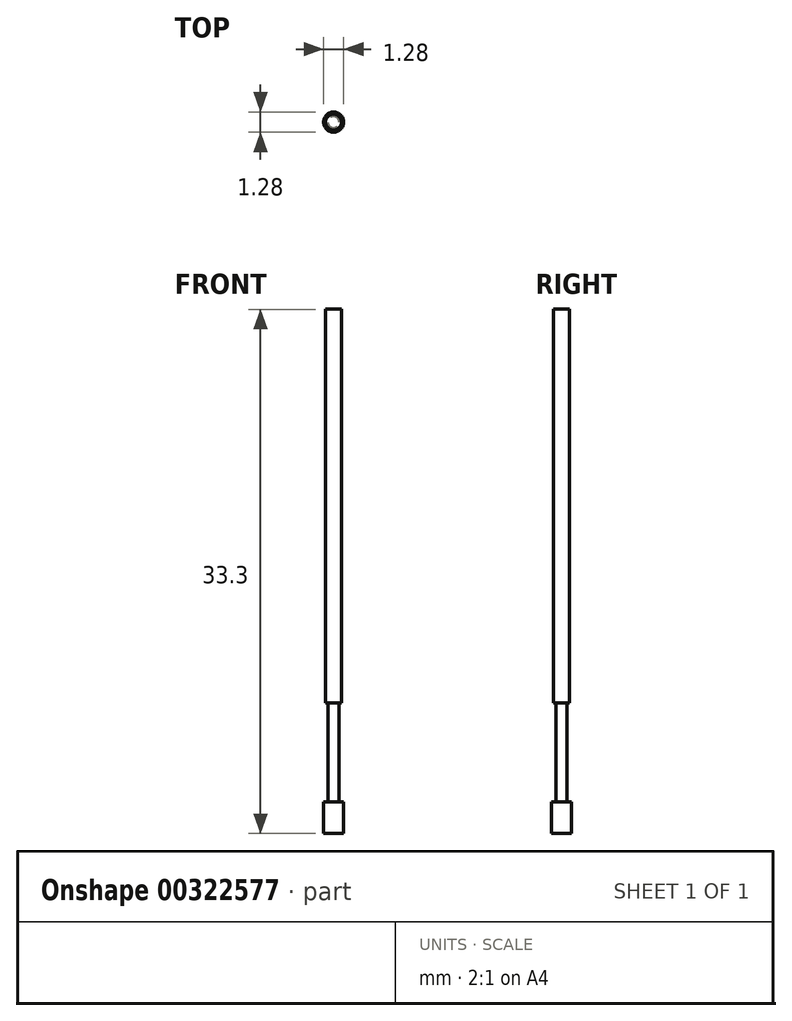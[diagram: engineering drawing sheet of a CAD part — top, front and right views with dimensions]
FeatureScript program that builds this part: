
annotation { "Feature Type Name" : "Feature", "Feature Type Description" : "" }
export const myFeature = defineFeature(function(context is Context, id is Id, definition is map)
    precondition{}
    {
        {
            var Q0;
            Q0=qCreatedBy(makeId("Top.planeOp"),FACE);
            var sketch = newSketch(context, id + "F0", { "sketchPlane" : qUnion([Q0])});
            skCircle(sketch, "E0", {"center": v(0, 0) * mm, "radius": 0.5 * mm});
            skSolve(sketch);
        }
        {
            var Q0;
            Q0 = qSketchRegion(id + "F0", true);
            extrude(context, id + "F1", {"entities" : qUnion([Q0]), "depth" : 25 * mm, "offsetDistance" : 25.4 * mm});
        }
        {
            var Q0;
            Q0=makeQuery(id+"F1.opExtrude","CAP_FACE",FACE,{"disambiguationData":[OSD([sQuery(id+"F0.wireOp",EDGE,"E0")])],"isStart":true});
            var sketch = newSketch(context, id + "F2", { "sketchPlane" : qUnion([Q0])});
            skCircle(sketch, "E1", {"center": v(0, 0) * mm, "radius": 0.36 * mm});
            skSolve(sketch);
        }
        {
            var Q0;
            Q0 = qSketchRegion(id + "F2", true);
            extrude(context, id + "F3", {"entities" : qUnion([Q0]), "operationType" : NewBodyOperationType.ADD, "depth" : 6.3 * mm, "offsetDistance" : 25.4 * mm});
        }
        {
            var Q0;
            Q0=makeQuery(id+"F3.opExtrude","CAP_FACE",FACE,{"disambiguationData":[OSD([sQuery(id+"F2.wireOp",EDGE,"E1")])],"isStart":false});
            var sketch = newSketch(context, id + "F4", { "sketchPlane" : qUnion([Q0])});
            skCircle(sketch, "E2", {"center": v(0, 0) * mm, "radius": 0.64 * mm});
            skSolve(sketch);
        }
        {
            var Q0;
            Q0 = qSketchRegion(id + "F4", true);
            extrude(context, id + "F5", {"entities" : qUnion([Q0]), "operationType" : NewBodyOperationType.ADD, "depth" : 2 * mm, "offsetDistance" : 25.4 * mm});
        }
    });
